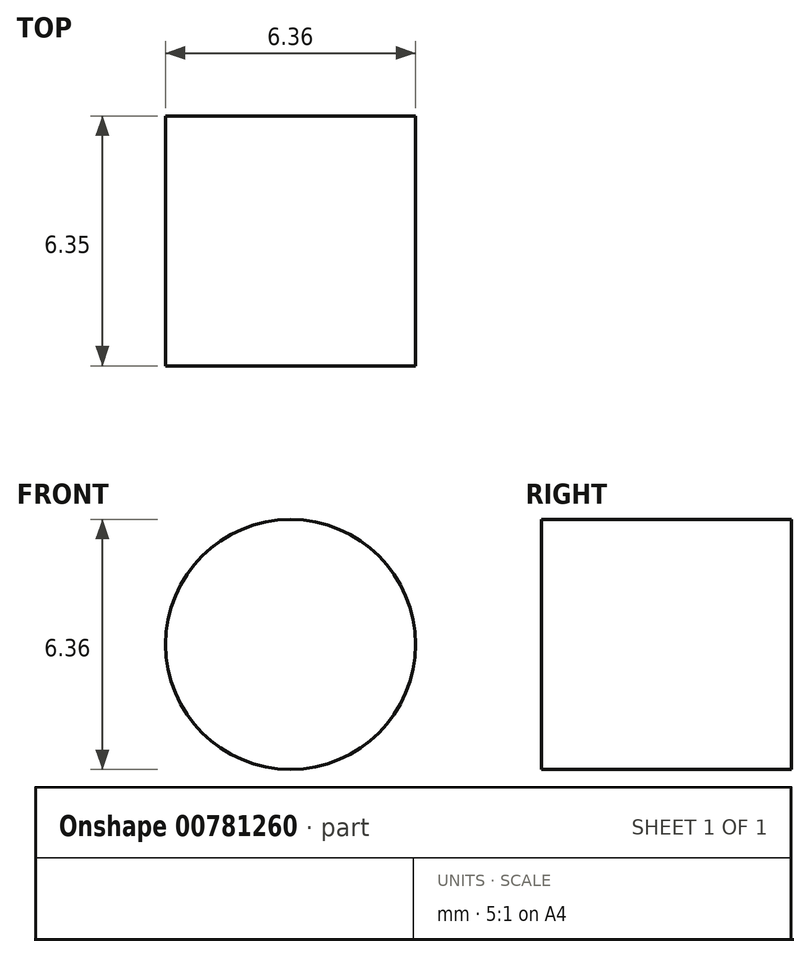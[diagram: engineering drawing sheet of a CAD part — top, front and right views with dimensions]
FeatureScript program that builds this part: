
annotation { "Feature Type Name" : "Feature", "Feature Type Description" : "" }
export const myFeature = defineFeature(function(context is Context, id is Id, definition is map)
    precondition{}
    {
        {
            var Q0;
            Q0=qCreatedBy(makeId("Front.planeOp"),FACE);
            var sketch = newSketch(context, id + "F0", { "sketchPlane" : qUnion([Q0])});
            skCircle(sketch, "E0", {"center": v(0, 0) * mm, "radius": 3.18 * mm});
            skSolve(sketch);
        }
        {
            var Q0;
            Q0=makeQuery(id+"F0.imprint","IMPRINT",FACE,{"disambiguationData":[TD([[makeQuery(id+"F0.imprint","IMPRINT",EDGE,{"derivedFrom":sQuery(id+"F0.wireOp",EDGE,"E0")}),1.0]])]});
            extrude(context, id + "F1", {"entities" : qUnion([Q0]), "depth" : 6.35 * mm, "offsetDistance" : 25.4 * mm});
        }
    });
